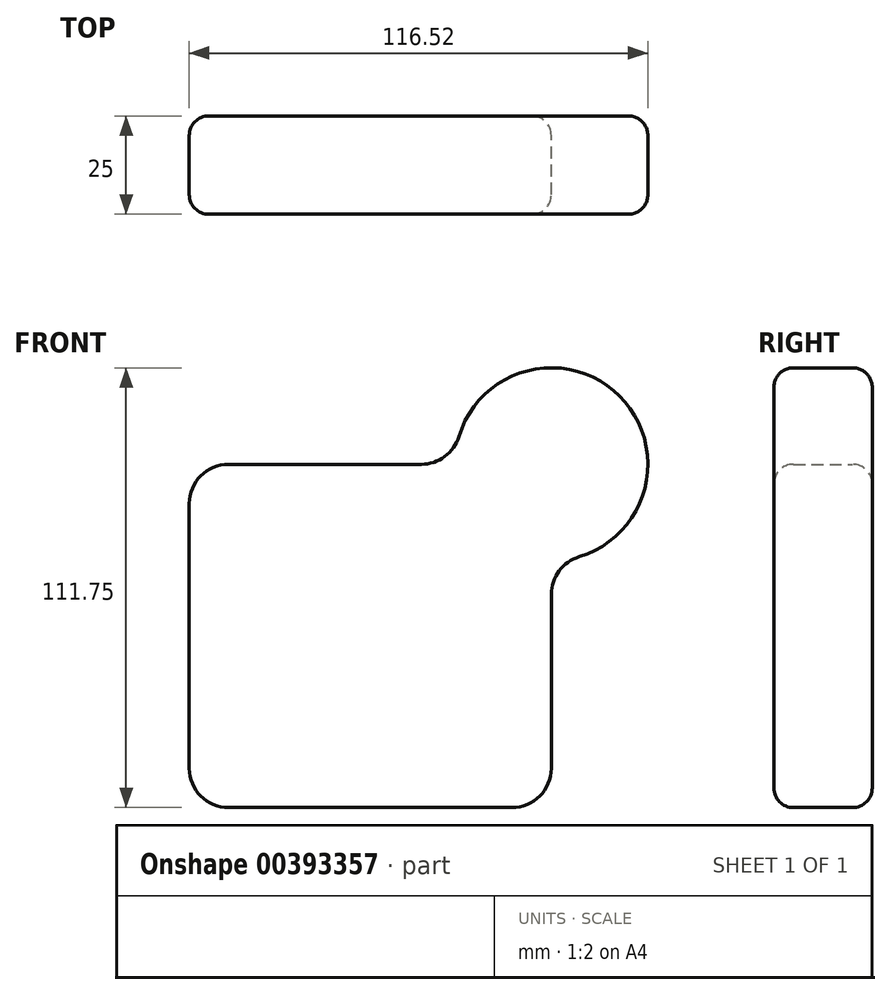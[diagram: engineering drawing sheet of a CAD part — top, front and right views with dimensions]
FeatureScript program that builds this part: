
annotation { "Feature Type Name" : "Feature", "Feature Type Description" : "" }
export const myFeature = defineFeature(function(context is Context, id is Id, definition is map)
    precondition{}
    {
        {
            var Q0;
            Q0=qCreatedBy(makeId("Front.planeOp"),FACE);
            var sketch = newSketch(context, id + "F0", { "sketchPlane" : qUnion([Q0])});
            skLineSegment(sketch, "E0.bottom", {"start": v(12.95, 43.61) * mm, "end": v(-36, 43.61) * mm});
            skLineSegment(sketch, "E0.top", {"start": v(36, -43.61) * mm, "end": v(-36, -43.61) * mm});
            skLineSegment(sketch, "E0.left", {"start": v(46, 10.57) * mm, "end": v(46, -33.61) * mm});
            skLineSegment(sketch, "E0.right", {"start": v(-46, 33.61) * mm, "end": v(-46, -33.61) * mm});
            skPoint(sketch, "E0.middle", {"position": v(0, 0) * mm});
            skArc(sketch, "E1", {"start": v(53.1, 20.14) * mm, "mid": v(63.34, 60.95) * mm, "end": v(22.52, 50.72) * mm});
            skPoint(sketch, "E2.visualSharp", {"position": v(-46, 43.61) * mm});
            skArc(sketch, "E2.filletArc", {"start": v(-36, 43.61) * mm, "mid": v(-43.07, 40.68) * mm, "end": v(-46, 33.61) * mm});
            skPoint(sketch, "E3.visualSharp", {"position": v(-46, -43.61) * mm});
            skArc(sketch, "E3.filletArc", {"start": v(-46, -33.61) * mm, "mid": v(-43.07, -40.68) * mm, "end": v(-36, -43.61) * mm});
            skPoint(sketch, "E4.visualSharp", {"position": v(46, -43.61) * mm});
            skArc(sketch, "E4.filletArc", {"start": v(36, -43.61) * mm, "mid": v(43.07, -40.68) * mm, "end": v(46, -33.61) * mm});
            skPoint(sketch, "E5.visualSharp", {"position": v(46, 19.09) * mm});
            skArc(sketch, "E5.filletArc", {"start": v(53.1, 20.14) * mm, "mid": v(47.97, 16.53) * mm, "end": v(46, 10.57) * mm});
            skPoint(sketch, "E6.visualSharp", {"position": v(21.47, 43.61) * mm});
            skArc(sketch, "E6.filletArc", {"start": v(12.95, 43.61) * mm, "mid": v(18.91, 45.58) * mm, "end": v(22.52, 50.72) * mm});
            skSolve(sketch);
        }
        {
            var Q0;
            Q0 = qSketchRegion(id + "F0", true);
            extrude(context, id + "F1", {"entities" : qUnion([Q0]), "depth" : 25 * mm});
        }
        {
            var Q0;
            Q0=makeQuery(id+"F1.opExtrude","CAP_EDGE",EDGE,{"disambiguationData":[OSD([sQuery(id+"F0.wireOp",EDGE,"E1")])],"isStart":false});
            var Q1;
            Q1=makeQuery(id+"F1.opExtrude","CAP_EDGE",EDGE,{"disambiguationData":[OSD([sQuery(id+"F0.wireOp",EDGE,"E1")])],"isStart":true});
            fillet(context, id + "F2", {"entities" : qUnion([Q0, Q1]), "radius" : 5 * mm, "tangentPropagation" : true, "allowEdgeOverflow" : false});
        }
        {
            var Q0;
            Q0=makeQuery(id+"F1.opExtrude","CAP_FACE",FACE,{"disambiguationData":[OSD([sQuery(id+"F0.wireOp",EDGE,"E0.bottom"),sQuery(id+"F0.wireOp",EDGE,"E0.top"),sQuery(id+"F0.wireOp",EDGE,"E0.left"),sQuery(id+"F0.wireOp",EDGE,"E0.right"),sQuery(id+"F0.wireOp",EDGE,"E1"),sQuery(id+"F0.wireOp",EDGE,"E2.filletArc"),sQuery(id+"F0.wireOp",EDGE,"E3.filletArc"),sQuery(id+"F0.wireOp",EDGE,"E4.filletArc"),sQuery(id+"F0.wireOp",EDGE,"E5.filletArc"),sQuery(id+"F0.wireOp",EDGE,"E6.filletArc")])],"isStart":false});
            var sketch = newSketch(context, id + "F3", { "sketchPlane" : qUnion([Q0])});
            skCircle(sketch, "E7", {"center": v(46, 43.61) * mm, "radius": 5 * mm});
            skSolve(sketch);
        }
        {
            var Q0;
            Q0=sQuery(id+"F3.wireOp",EDGE,"E7");
            extrude(context, id + "F4", {"bodyType" : ToolBodyType.SURFACE, "surfaceEntities" : qUnion([Q0]), "oppositeDirection" : true, "depth" : 25 * mm});
        }
        {
            var Q0;
            Q0=makeQuery(id+"F4.opExtrude","SWEPT_BODY",BODY,{"disambiguationData":[OSD([sQuery(id+"F3.wireOp",EDGE,"E7")])]});
            deleteBodies(context, id + "F5", {"entities" : qUnion([Q0])});
        }
    });
